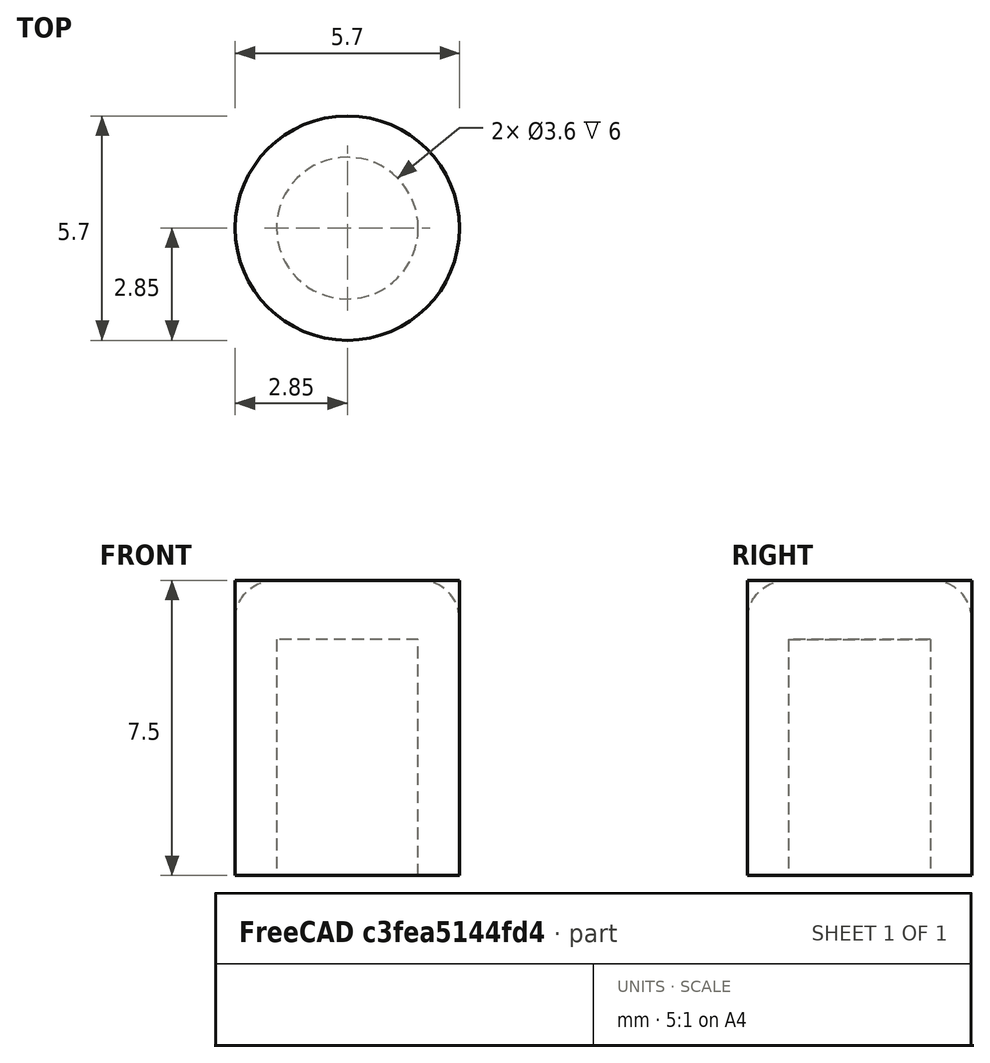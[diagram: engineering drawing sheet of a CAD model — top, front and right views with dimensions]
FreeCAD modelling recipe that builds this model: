
FCSTD DOCUMENT  (FreeCAD 0.20R29603 (Git))
Label: nowyguzik
License: All rights reserved
LicenseURL: http://en.wikipedia.org/wiki/All_rights_reserved
objects: Sketcher::SketchObject×2, PartDesign::Pad×1, PartDesign::Pocket×1, PartDesign::Body×1, Part::Fillet×1, Mesh::Feature×1
note: 8 computed .brp shape members not serialized (recipe doc carries the construction recipe); baked Part::Feature solids carry a one-line shape summary decoded from their .brp

FEATURE [Sketcher::SketchObject] Sketch
  FullyConstrained = true
  MapMode = 5
  Support = -> [XY_Plane]
  sketch-geometry (1):
    g0: Circle CenterX=0 CenterY=0 CenterZ=0 NormalX=0 NormalY=0 NormalZ=1 AngleXU=0 Radius=2.85
  constraints (2):
    c: Coincident(g0,g-1)
    c: Diameter(g0) = 5.7
FEATURE [PartDesign::Pad] Pad
  Direction = (0,0,1)
  Length = 7.5
  Length2 = 10
  Profile = -> Sketch
  ReferenceAxis = -> Sketch [N_Axis]
  Type = 0
FEATURE [Sketcher::SketchObject] Sketch001
  FullyConstrained = true
  MapMode = 5
  Placement = pos=(0,0,0) rot=(1,0,0;3.14159rad)
  Support = -> [Pad]
  sketch-geometry (1):
    g0: Circle CenterX=0 CenterY=0 CenterZ=0 NormalX=0 NormalY=0 NormalZ=1 AngleXU=0 Radius=1.8
  constraints (2):
    c: Coincident(g0,g-1)
    c: Diameter(g0) = 3.6
FEATURE [PartDesign::Pocket] Pocket
  BaseFeature = -> Pad
  Direction = (0,0,1)
  Length = 6
  Length2 = 5
  Profile = -> Sketch001
  ReferenceAxis = -> Sketch001 [N_Axis]
  Type = 0
FEATURE [PartDesign::Body] Body
  Group = -> [Sketch,Pad,Sketch001,Pocket]
  Origin = -> Origin
  Tip = -> Pocket
FEATURE [Part::Fillet] Fillet
  Base = -> Pocket
  Edges = 1 edges r=1: [Edge3]
FEATURE [Mesh::Feature] Mesh  label="Fillet (Meshed)"
